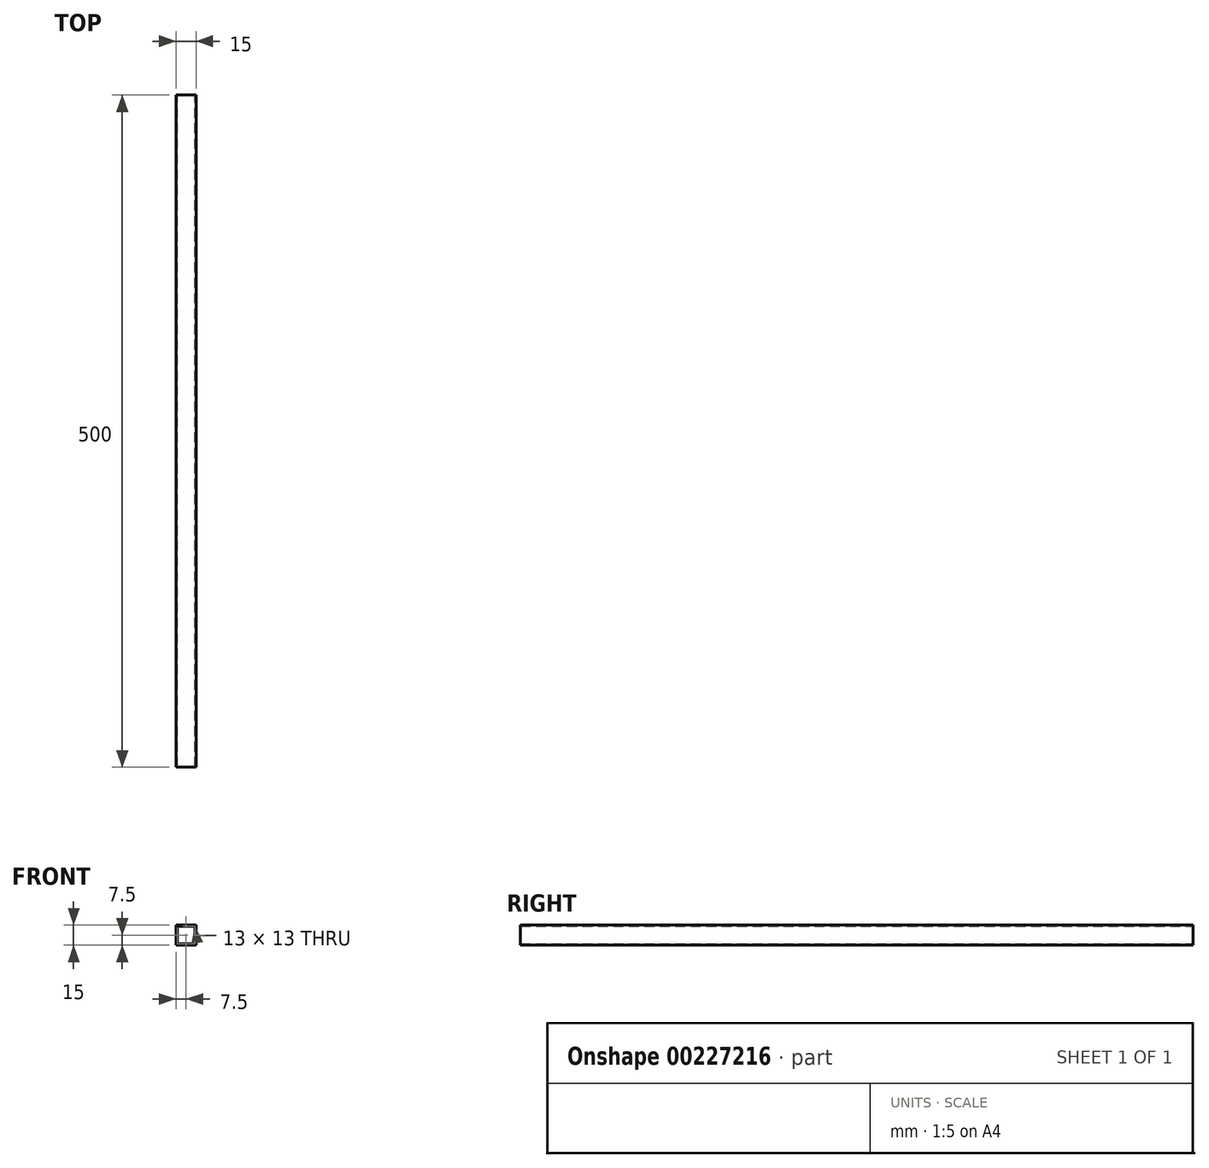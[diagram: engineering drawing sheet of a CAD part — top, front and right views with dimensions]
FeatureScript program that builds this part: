
annotation { "Feature Type Name" : "Feature", "Feature Type Description" : "" }
export const myFeature = defineFeature(function(context is Context, id is Id, definition is map)
    precondition{}
    {
        {
            var Q0;
            Q0=qCreatedBy(makeId("Front.planeOp"),FACE);
            var sketch = newSketch(context, id + "F0", { "sketchPlane" : qUnion([Q0])});
            skLineSegment(sketch, "E0.bottom", {"start": v(7.5, -7.5) * mm, "end": v(-7.5, -7.5) * mm});
            skLineSegment(sketch, "E0.top", {"start": v(7.5, 7.5) * mm, "end": v(-7.5, 7.5) * mm});
            skLineSegment(sketch, "E0.left", {"start": v(7.5, -7.5) * mm, "end": v(7.5, 7.5) * mm});
            skLineSegment(sketch, "E0.right", {"start": v(-7.5, -7.5) * mm, "end": v(-7.5, 7.5) * mm});
            skPoint(sketch, "E0.middle", {"position": v(0, 0) * mm});
            skLineSegment(sketch, "E1.bottom", {"start": v(6.5, -6.5) * mm, "end": v(-6.5, -6.5) * mm});
            skLineSegment(sketch, "E1.top", {"start": v(6.5, 6.5) * mm, "end": v(-6.5, 6.5) * mm});
            skLineSegment(sketch, "E1.left", {"start": v(6.5, -6.5) * mm, "end": v(6.5, 6.5) * mm});
            skLineSegment(sketch, "E1.right", {"start": v(-6.5, -6.5) * mm, "end": v(-6.5, 6.5) * mm});
            skSolve(sketch);
        }
        {
            var Q0;
            Q0 = qSketchRegion(id + "F0", true);
            extrude(context, id + "F1", {"entities" : qUnion([Q0]), "endBound" : BoundingType.SYMMETRIC, "depth" : 500 * mm});
        }
    });
